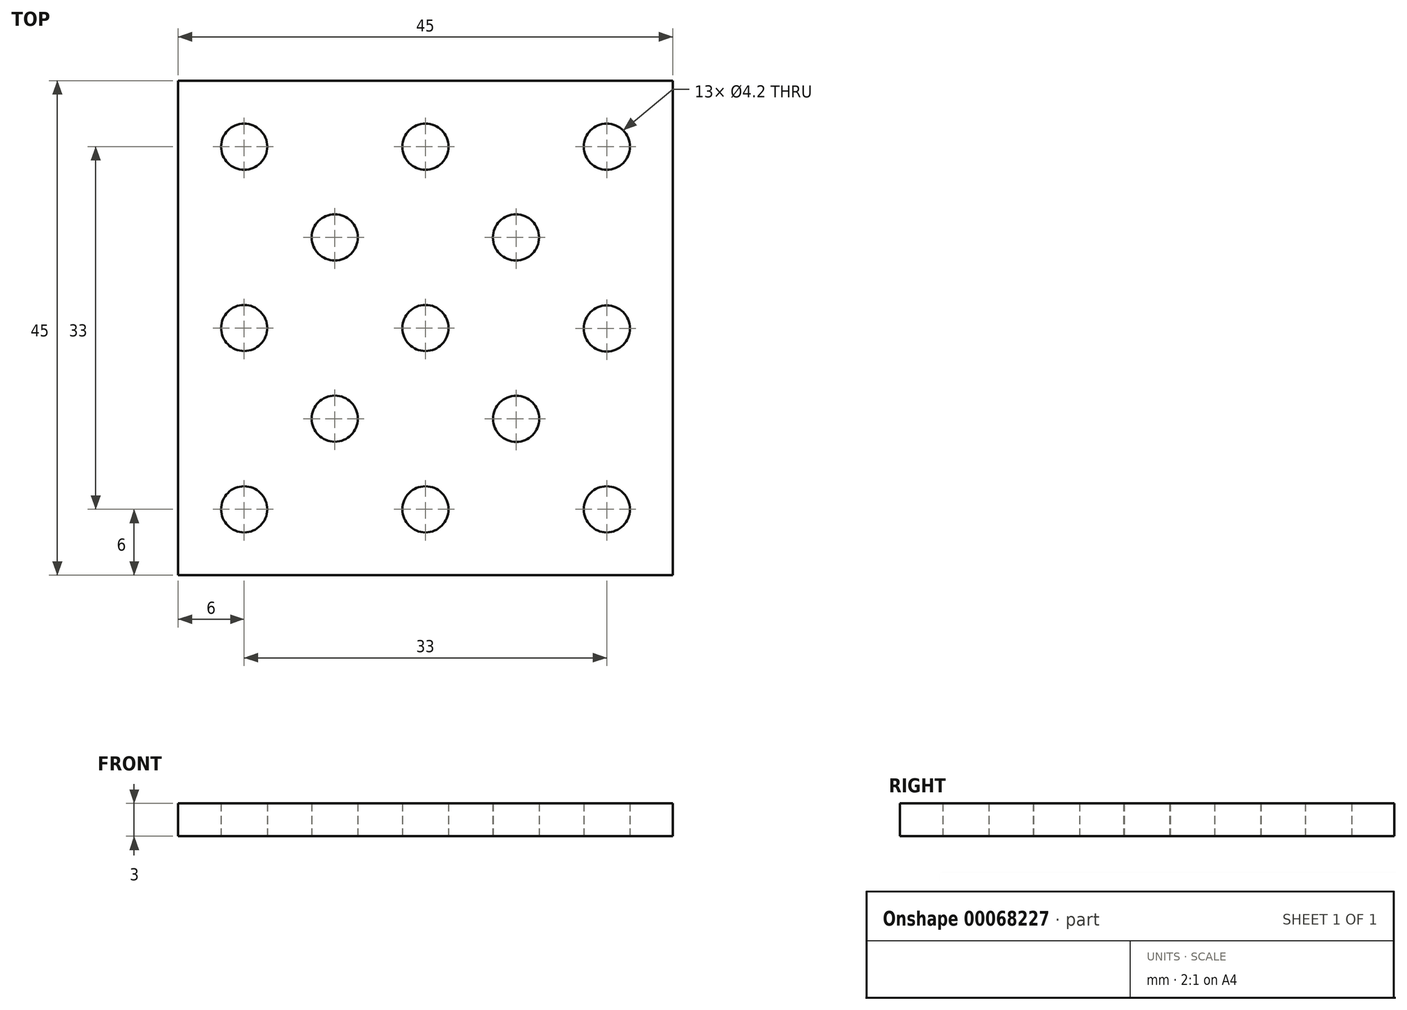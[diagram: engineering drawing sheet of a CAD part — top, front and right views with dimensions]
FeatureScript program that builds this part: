
annotation { "Feature Type Name" : "Feature", "Feature Type Description" : "" }
export const myFeature = defineFeature(function(context is Context, id is Id, definition is map)
    precondition{}
    {
        {
            var Q0;
            Q0=qCreatedBy(makeId("Top.planeOp"),FACE);
            var sketch = newSketch(context, id + "F0", { "sketchPlane" : qUnion([Q0])});
            skLineSegment(sketch, "E0.rect.bottom", {"start": v(-22.5, 22.5) * mm, "end": v(22.5, 22.5) * mm});
            skLineSegment(sketch, "E0.rect.top", {"start": v(-22.5, -22.5) * mm, "end": v(22.5, -22.5) * mm});
            skLineSegment(sketch, "E0.rect.left", {"start": v(-22.5, 22.5) * mm, "end": v(-22.5, -22.5) * mm});
            skLineSegment(sketch, "E0.rect.right", {"start": v(22.5, 22.5) * mm, "end": v(22.5, -22.5) * mm});
            skPoint(sketch, "E0.rect.middle", {"position": v(0, 0) * mm});
            skCircle(sketch, "E1", {"center": v(-16.5, 16.5) * mm, "radius": 2.1 * mm});
            skCircle(sketch, "E2.MirrorC", {"center": v(16.5, 16.5) * mm, "radius": 2.1 * mm});
            skCircle(sketch, "E3.MirrorC", {"center": v(16.5, -16.5) * mm, "radius": 2.1 * mm});
            skCircle(sketch, "E4.MirrorC", {"center": v(-16.5, -16.5) * mm, "radius": 2.1 * mm});
            skCircle(sketch, "E5.MirrorC", {"center": v(16.5, -0.05) * mm, "radius": 2.1 * mm});
            skLineSegment(sketch, "E6", {"start": v(16.5, 16.5) * mm, "end": v(16.5, -16.5) * mm, "construction": true});
            skLineSegment(sketch, "E7", {"start": v(16.5, -16.5) * mm, "end": v(-16.5, -16.5) * mm, "construction": true});
            skLineSegment(sketch, "E8", {"start": v(-16.5, -16.5) * mm, "end": v(-16.5, 16.5) * mm, "construction": true});
            skLineSegment(sketch, "E9", {"start": v(-16.5, 16.5) * mm, "end": v(16.5, 16.5) * mm, "construction": true});
            skCircle(sketch, "E10.MirrorC", {"center": v(0, -16.5) * mm, "radius": 2.1 * mm});
            skLineSegment(sketch, "E11", {"start": v(-16.5, 0) * mm, "end": v(0, -16.5) * mm, "construction": true});
            skLineSegment(sketch, "E12", {"start": v(16.5, -0.05) * mm, "end": v(0, -16.5) * mm, "construction": true});
            skLineSegment(sketch, "E13", {"start": v(16.5, -0.05) * mm, "end": v(0, 16.5) * mm, "construction": true});
            skLineSegment(sketch, "E14", {"start": v(-16.5, -16.5) * mm, "end": v(16.5, 16.5) * mm, "construction": true});
            skPoint(sketch, "E15", {"position": v(8.24, 8.24) * mm});
            skPoint(sketch, "E16", {"position": v(-8.25, -8.25) * mm});
            skCircle(sketch, "E17.MirrorC", {"center": v(-8.25, -8.25) * mm, "radius": 2.1 * mm});
            skCircle(sketch, "E18.MirrorC", {"center": v(8.24, 8.24) * mm, "radius": 2.1 * mm});
            skLineSegment(sketch, "E19", {"start": v(-16.5, 16.5) * mm, "end": v(16.5, -16.5) * mm, "construction": true});
            skPoint(sketch, "E20", {"position": v(8.26, -8.26) * mm});
            skCircle(sketch, "E21.MirrorC", {"center": v(8.26, -8.26) * mm, "radius": 2.1 * mm});
            skLineSegment(sketch, "E22.bottom", {"start": v(-22.5, 22.5) * mm, "end": v(7.5, 22.5) * mm, "construction": true});
            skLineSegment(sketch, "E22.top", {"start": v(-22.5, -7.5) * mm, "end": v(7.5, -7.5) * mm, "construction": true});
            skLineSegment(sketch, "E22.left", {"start": v(-22.5, 22.5) * mm, "end": v(-22.5, -7.5) * mm, "construction": true});
            skLineSegment(sketch, "E22.right", {"start": v(7.5, 22.5) * mm, "end": v(7.5, -7.5) * mm, "construction": true});
            skCircle(sketch, "E23.MirrorC", {"center": v(0, 0) * mm, "radius": 2.1 * mm});
            skPoint(sketch, "E24", {"position": v(-16.5, 0) * mm});
            skCircle(sketch, "E25.MirrorC", {"center": v(-16.5, 0) * mm, "radius": 2.1 * mm});
            skLineSegment(sketch, "E26", {"start": v(-16.5, 0) * mm, "end": v(0, 16.5) * mm, "construction": true});
            skPoint(sketch, "E27", {"position": v(-8.25, 8.25) * mm});
            skCircle(sketch, "E28", {"center": v(-8.25, 8.25) * mm, "radius": 2.1 * mm});
            skCircle(sketch, "E29", {"center": v(0, 16.5) * mm, "radius": 2.1 * mm});
            skSolve(sketch);
        }
        {
            var Q0;
            Q0=qSketchRegion(id+"F0",true);
            extrude(context, id + "F1", {"entities" : qUnion([Q0]), "depth" : 3 * mm});
        }
    });
